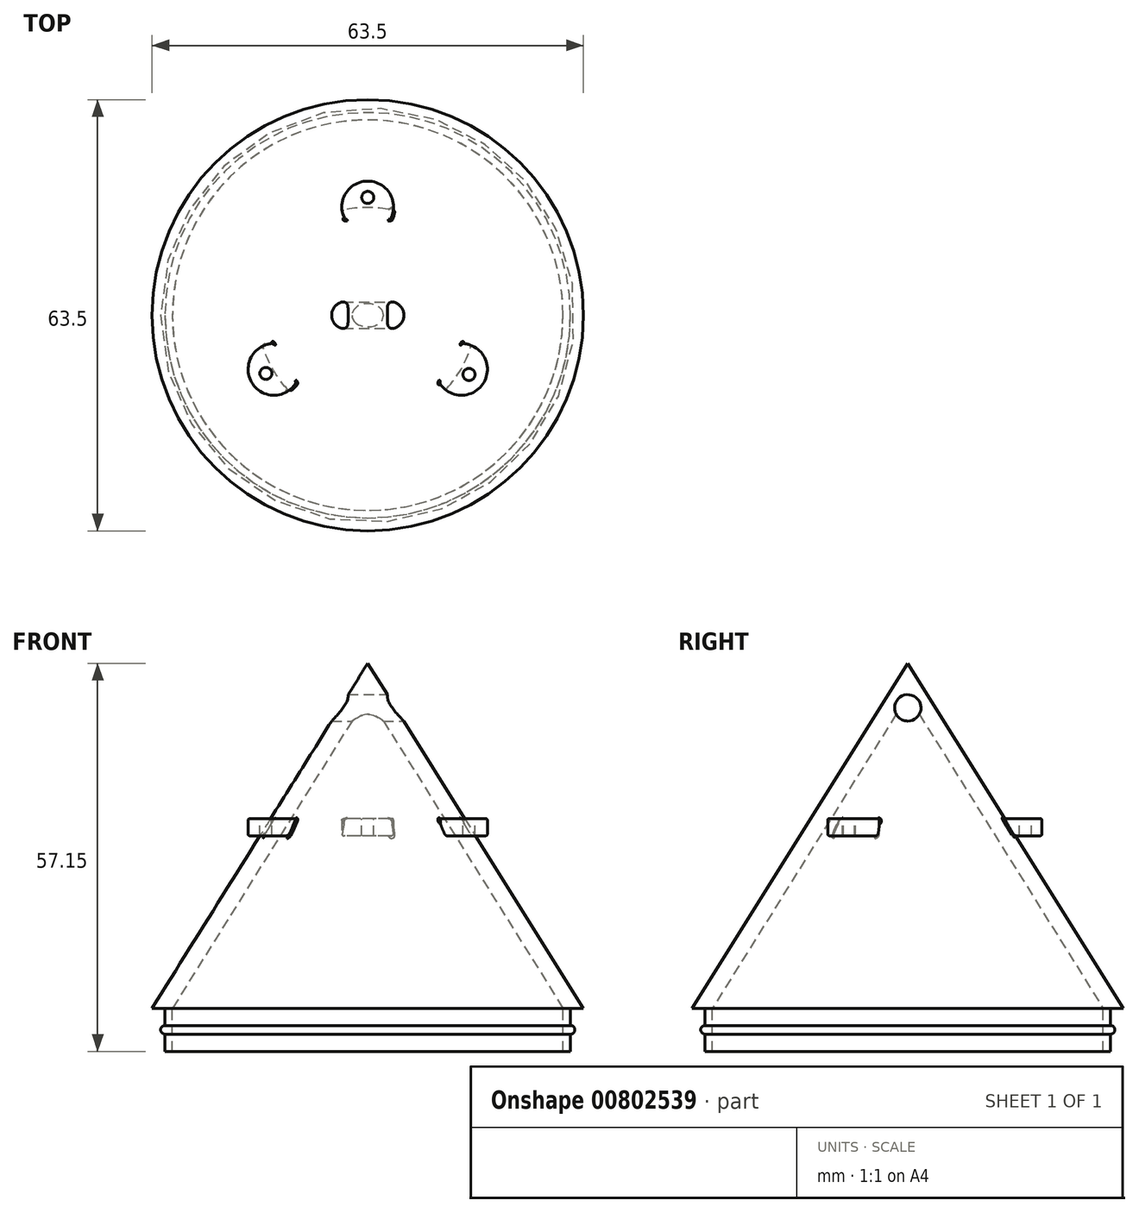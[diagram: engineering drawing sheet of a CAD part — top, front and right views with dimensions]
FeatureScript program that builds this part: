
annotation { "Feature Type Name" : "Feature", "Feature Type Description" : "" }
export const myFeature = defineFeature(function(context is Context, id is Id, definition is map)
    precondition{}
    {
        {
            var Q0;
            Q0=qCreatedBy(makeId("Front.planeOp"),FACE);
            var sketch = newSketch(context, id + "F0", { "sketchPlane" : qUnion([Q0])});
            skLineSegment(sketch, "E0", {"start": v(0, 50.8) * mm, "end": v(31.75, 0) * mm});
            skPoint(sketch, "E1.end.orphan", {"position": v(61.88, 0) * mm});
            skLineSegment(sketch, "E2", {"start": v(0, 0) * mm, "end": v(31.75, 0) * mm});
            skLineSegment(sketch, "E3", {"start": v(0, 50.8) * mm, "end": v(0, 0) * mm});
            skSolve(sketch);
        }
        {
            var Q0;
            Q0=makeQuery(id+"F0.imprint","IMPRINT",FACE,{"disambiguationData":[TD([[makeQuery(id+"F0.imprint","IMPRINT",EDGE,{"derivedFrom":sQuery(id+"F0.wireOp",EDGE,"E0")}),-1.0]])]});
            var Q1;
            Q1=sQuery(id+"F0.wireOp",EDGE,"E3");
            revolve(context, id + "F1", {"surfaceOperationType" : NewSurfaceOperationType.NEW, "entities" : qUnion([Q0]), "axis" : qUnion([Q1]), "revolveType" : RevolveType.FULL});
        }
        {
            var Q0;
            Q0=makeQuery(id+"F1.opRevolve","SWEPT_FACE",FACE,{"disambiguationData":[OSD([sQuery(id+"F0.wireOp",EDGE,"E2")])]});
            shell(context, id + "F2", {"entities" : qUnion([Q0]), "thickness" : 2.54 * mm});
        }
        {
            var Q0;
            Q0=makeQuery(id+"F1.opRevolve","SWEPT_FACE",FACE,{"disambiguationData":[OSD([sQuery(id+"F0.wireOp",EDGE,"E2")])]});
            var sketch = newSketch(context, id + "F3", { "sketchPlane" : qUnion([Q0])});
            skCircle(sketch, "E4", {"center": v(0, 0) * mm, "radius": 29.85 * mm});
            skCircle(sketch, "E5", {"center": v(0, 0) * mm, "radius": 28.58 * mm});
            skSolve(sketch);
        }
        {
            var Q0;
            Q0=makeQuery(id+"F3.imprint","IMPRINT",FACE,{"disambiguationData":[TD([[makeQuery(id+"F3.imprint","IMPRINT",EDGE,{"derivedFrom":sQuery(id+"F3.wireOp",EDGE,"E4")}),1.0]])]});
            extrude(context, id + "F4", {"entities" : qUnion([Q0]), "operationType" : NewBodyOperationType.ADD, "depth" : 6.35 * mm, "offsetDistance" : 25.4 * mm});
        }
        {
            var Q0;
            Q0=makeQuery(id+"F1.opRevolve","SWEPT_FACE",FACE,{"disambiguationData":[OSD([sQuery(id+"F0.wireOp",EDGE,"E2")])]});
            cPlane(context, id + "F5", {"entities" : qUnion([Q0]), "cplaneType" : CPlaneType.OFFSET, "offset" : 3.17 * mm, "width" : 152.4 * mm, "height" : 152.4 * mm});
        }
        {
            var Q0;
            Q0=qCreatedBy(id+"F5.planeOp",FACE);
            var sketch = newSketch(context, id + "F6", { "sketchPlane" : qUnion([Q0])});
            skCircle(sketch, "E6", {"center": v(0, 0) * mm, "radius": 29.85 * mm});
            skSolve(sketch);
        }
        {
            var Q0;
            Q0=qCreatedBy(makeId("Right.planeOp"),FACE);
            var sketch = newSketch(context, id + "F7", { "sketchPlane" : qUnion([Q0])});
            skCircle(sketch, "E7", {"center": v(-29.86, -3.18) * mm, "radius": 0.64 * mm});
            skSolve(sketch);
        }
        {
            var Q0;
            Q0=makeQuery(id+"F7.imprint","IMPRINT",FACE,{"disambiguationData":[TD([[makeQuery(id+"F7.imprint","IMPRINT",EDGE,{"derivedFrom":sQuery(id+"F7.wireOp",EDGE,"E7")}),1.0]])]});
            var Q1;
            Q1=sQuery(id+"F6.wireOp",EDGE,"E6");
            sweep(context, id + "F8", {"operationType" : NewBodyOperationType.ADD, "profiles" : qUnion([Q0]), "path" : qUnion([Q1])});
        }
        {
            var Q0;
            Q0=qCreatedBy(makeId("Right.planeOp"),FACE);
            var sketch = newSketch(context, id + "F9", { "sketchPlane" : qUnion([Q0])});
            skCircle(sketch, "E8", {"center": v(0, 44.24) * mm, "radius": 1.94 * mm});
            skSolve(sketch);
        }
        {
            var Q0;
            Q0 = qSketchRegion(id + "F9", true);
            extrude(context, id + "F10", {"entities" : qUnion([Q0]), "operationType" : NewBodyOperationType.REMOVE, "endBound" : BoundingType.THROUGH_ALL, "oppositeDirection" : true, "depth" : 25.4 * mm, "offsetDistance" : 25.4 * mm, "hasSecondDirection" : true, "secondDirectionBound" : SecondDirectionBoundingType.THROUGH_ALL, "secondDirectionOppositeDirection" : false, "secondDirectionDepth" : 25.4 * mm});
        }
        {
            var Q0;
            Q0=qCreatedBy(makeId("Top.planeOp"),FACE);
            cPlane(context, id + "F11", {"entities" : qUnion([Q0]), "cplaneType" : CPlaneType.OFFSET, "offset" : 25.4 * mm, "width" : 152.4 * mm, "height" : 152.4 * mm});
        }
        {
            var Q0;
            Q0=qCreatedBy(makeId("Right.planeOp"),FACE);
            var sketch = newSketch(context, id + "F12", { "sketchPlane" : qUnion([Q0])});
            skLineSegment(sketch, "E9", {"start": v(-15.8, 25.4) * mm, "end": v(15.94, 25.4) * mm});
            skSolve(sketch);
        }
        {
            var Q0;
            Q0=qCreatedBy(id+"F11.planeOp",FACE);
            var sketch = newSketch(context, id + "F13", { "sketchPlane" : qUnion([Q0])});
            skLineSegment(sketch, "E10", {"start": v(0, 15.94) * mm, "end": v(-13.8, -7.97) * mm, "construction": true});
            skLineSegment(sketch, "E11", {"start": v(-13.8, -7.97) * mm, "end": v(13.8, -7.97) * mm, "construction": true});
            skLineSegment(sketch, "E12", {"start": v(13.8, -7.97) * mm, "end": v(0, 15.94) * mm, "construction": true});
            skLineSegment(sketch, "E13.0", {"start": v(0, -15.8) * mm, "end": v(0, 15.94) * mm});
            skArc(sketch, "E14", {"start": v(3.04, 13.64) * mm, "mid": v(0, 19.75) * mm, "end": v(-3.04, 13.64) * mm});
            skArc(sketch, "E15", {"start": v(10.3, -9.45) * mm, "mid": v(17.1, -9.87) * mm, "end": v(13.33, -4.19) * mm});
            skArc(sketch, "E16", {"start": v(-13.33, -4.19) * mm, "mid": v(-17.1, -9.87) * mm, "end": v(-10.3, -9.45) * mm});
            skArc(sketch, "E17", {"start": v(-13.33, -4.19) * mm, "mid": v(-12.1, -6.99) * mm, "end": v(-10.3, -9.45) * mm});
            skArc(sketch, "E18.trimOffspring", {"start": v(3.04, 13.64) * mm, "mid": v(0, 13.97) * mm, "end": v(-3.04, 13.64) * mm});
            skArc(sketch, "E19.trimOffspring", {"start": v(10.3, -9.45) * mm, "mid": v(12.1, -6.99) * mm, "end": v(13.33, -4.19) * mm});
            skSolve(sketch);
        }
        {
            var Q0;
            Q0=makeQuery(id+"F13.imprint","IMPRINT",FACE,{"disambiguationData":[TD([[makeQuery(id+"F13.imprint","IMPRINT",EDGE,{"derivedFrom":sQuery(id+"F13.wireOp",EDGE,"E16")}),1.0]])]});
            var Q1;
            {var subQ0=sQuery(id+"F13.wireOp",EDGE,"E14");Q1=makeQuery(id+"F13.imprint","IMPRINT",FACE,{"disambiguationData":[TD([[makeQuery(id+"F13.imprint","IMPRINT",EDGE,{"derivedFrom":subQ0}),1.0]])]});}
            var Q2;
            Q2=makeQuery(id+"F13.imprint","IMPRINT",FACE,{"disambiguationData":[TD([[makeQuery(id+"F13.imprint","IMPRINT",EDGE,{"derivedFrom":sQuery(id+"F13.wireOp",EDGE,"E15")}),1.0]])]});
            extrude(context, id + "F14", {"entities" : qUnion([Q0, Q1, Q2]), "operationType" : NewBodyOperationType.ADD, "depth" : 2.54 * mm, "offsetDistance" : 25.4 * mm});
        }
        {
            var Q0;
            Q0=makeQuery(id+"F14.opExtrude","CAP_FACE",FACE,{"disambiguationData":[OSD([sQuery(id+"F13.wireOp",EDGE,"E15"),sQuery(id+"F13.wireOp",EDGE,"E19.trimOffspring")])],"isStart":false});
            cPlane(context, id + "F15", {"entities" : qUnion([Q0]), "cplaneType" : CPlaneType.OFFSET, "offset" : 0 * mm, "width" : 152.4 * mm, "height" : 152.4 * mm});
        }
        {
            var Q0;
            Q0=qCreatedBy(id+"F15.planeOp",FACE);
            var sketch = newSketch(context, id + "F16", { "sketchPlane" : qUnion([Q0])});
            skCircle(sketch, "E20", {"center": v(0, 17.34) * mm, "radius": 0.89 * mm});
            skCircle(sketch, "E21", {"center": v(14.9, -8.72) * mm, "radius": 0.89 * mm});
            skCircle(sketch, "E22", {"center": v(-15, -8.58) * mm, "radius": 0.89 * mm});
            skSolve(sketch);
        }
        {
            var Q0;
            Q0 = qSketchRegion(id + "F16", true);
            extrude(context, id + "F17", {"entities" : qUnion([Q0]), "operationType" : NewBodyOperationType.REMOVE, "endBound" : BoundingType.UP_TO_NEXT, "oppositeDirection" : true, "depth" : 1.27 * mm, "offsetDistance" : 25.4 * mm});
        }
        {
            var Q0;
            Q0=makeQuery(id+"F14.boolean.opBoolean","INTERSECT",EDGE,{"derivedFrom":[makeQuery(id+"F1.opRevolve","SWEPT_FACE",FACE,{"disambiguationData":[OSD([sQuery(id+"F0.wireOp",EDGE,"E0")])]}),makeQuery(id+"F14.opExtrude","CAP_FACE",FACE,{"disambiguationData":[OSD([sQuery(id+"F13.wireOp",EDGE,"E16"),sQuery(id+"F13.wireOp",EDGE,"E17")])],"isStart":true})]});
            var Q1;
            Q1=makeQuery(id+"F14.boolean.opBoolean","INTERSECT",EDGE,{"disambiguationData":[OD(1.0)],"derivedFrom":[makeQuery(id+"F1.opRevolve","SWEPT_FACE",FACE,{"disambiguationData":[OSD([sQuery(id+"F0.wireOp",EDGE,"E0")])]}),makeQuery(id+"F14.opExtrude","SWEPT_FACE",FACE,{"disambiguationData":[OSD([sQuery(id+"F13.wireOp",EDGE,"E16")])]})]});
            var Q2;
            Q2=makeQuery(id+"F14.boolean.opBoolean","INTERSECT",EDGE,{"derivedFrom":[makeQuery(id+"F1.opRevolve","SWEPT_FACE",FACE,{"disambiguationData":[OSD([sQuery(id+"F0.wireOp",EDGE,"E0")])]}),makeQuery(id+"F14.opExtrude","CAP_FACE",FACE,{"disambiguationData":[OSD([sQuery(id+"F13.wireOp",EDGE,"E16"),sQuery(id+"F13.wireOp",EDGE,"E17")])],"isStart":false})]});
            var Q3;
            Q3=makeQuery(id+"F14.opExtrude","CAP_EDGE",EDGE,{"disambiguationData":[OSD([sQuery(id+"F13.wireOp",EDGE,"E16")])],"isStart":false});
            var Q4;
            Q4=makeQuery(id+"F14.opExtrude","CAP_EDGE",EDGE,{"disambiguationData":[OSD([sQuery(id+"F13.wireOp",EDGE,"E16")])],"isStart":true});
            var Q5;
            Q5=makeQuery(id+"F14.opExtrude","CAP_EDGE",EDGE,{"disambiguationData":[OSD([sQuery(id+"F13.wireOp",EDGE,"E15")])],"isStart":false});
            var Q6;
            Q6=makeQuery(id+"F14.opExtrude","CAP_EDGE",EDGE,{"disambiguationData":[OSD([sQuery(id+"F13.wireOp",EDGE,"E15")])],"isStart":true});
            var Q7;
            Q7=makeQuery(id+"F14.boolean.opBoolean","INTERSECT",EDGE,{"derivedFrom":[makeQuery(id+"F1.opRevolve","SWEPT_FACE",FACE,{"disambiguationData":[OSD([sQuery(id+"F0.wireOp",EDGE,"E0")])]}),makeQuery(id+"F14.opExtrude","CAP_FACE",FACE,{"disambiguationData":[OSD([sQuery(id+"F13.wireOp",EDGE,"E15"),sQuery(id+"F13.wireOp",EDGE,"E19.trimOffspring")])],"isStart":false})]});
            var Q8;
            Q8=makeQuery(id+"F14.boolean.opBoolean","INTERSECT",EDGE,{"derivedFrom":[makeQuery(id+"F1.opRevolve","SWEPT_FACE",FACE,{"disambiguationData":[OSD([sQuery(id+"F0.wireOp",EDGE,"E0")])]}),makeQuery(id+"F14.opExtrude","CAP_FACE",FACE,{"disambiguationData":[OSD([sQuery(id+"F13.wireOp",EDGE,"E14"),sQuery(id+"F13.wireOp",EDGE,"E18.trimOffspring")])],"isStart":false})]});
            var Q9;
            Q9=makeQuery(id+"F14.boolean.opBoolean","INTERSECT",EDGE,{"disambiguationData":[OD(1.0)],"derivedFrom":[makeQuery(id+"F1.opRevolve","SWEPT_FACE",FACE,{"disambiguationData":[OSD([sQuery(id+"F0.wireOp",EDGE,"E0")])]}),makeQuery(id+"F14.opExtrude","SWEPT_FACE",FACE,{"disambiguationData":[OSD([sQuery(id+"F13.wireOp",EDGE,"E14")])]})]});
            var Q10;
            Q10=makeQuery(id+"F14.opExtrude","CAP_EDGE",EDGE,{"disambiguationData":[OSD([sQuery(id+"F13.wireOp",EDGE,"E14")])],"isStart":false});
            var Q11;
            Q11=makeQuery(id+"F14.opExtrude","CAP_EDGE",EDGE,{"disambiguationData":[OSD([sQuery(id+"F13.wireOp",EDGE,"E14")])],"isStart":true});
            var Q12;
            Q12=makeQuery(id+"F17.boolean.opBoolean","COPY",EDGE,{"derivedFrom":makeQuery(id+"F17.opExtrude","CAP_EDGE",EDGE,{"disambiguationData":[OSD([sQuery(id+"F16.wireOp",EDGE,"E20")])],"isStart":true})});
            var Q13;
            Q13=makeQuery(id+"F17.boolean.opBoolean","COPY",EDGE,{"derivedFrom":makeQuery(id+"F17.opExtrude","CAP_EDGE",EDGE,{"disambiguationData":[OSD([sQuery(id+"F16.wireOp",EDGE,"E22")])],"isStart":true})});
            var Q14;
            Q14=makeQuery(id+"F17.boolean.opBoolean","COPY",EDGE,{"derivedFrom":makeQuery(id+"F17.opExtrude","CAP_EDGE",EDGE,{"disambiguationData":[OSD([sQuery(id+"F16.wireOp",EDGE,"E21")])],"isStart":true})});
            fillet(context, id + "F18", {"entities" : qUnion([Q0, Q1, Q2, Q3, Q4, Q5, Q6, Q7, Q8, Q9, Q10, Q11, Q12, Q13, Q14]), "radius" : 0.25 * mm, "tangentPropagation" : true, "allowEdgeOverflow" : false});
        }
    });
